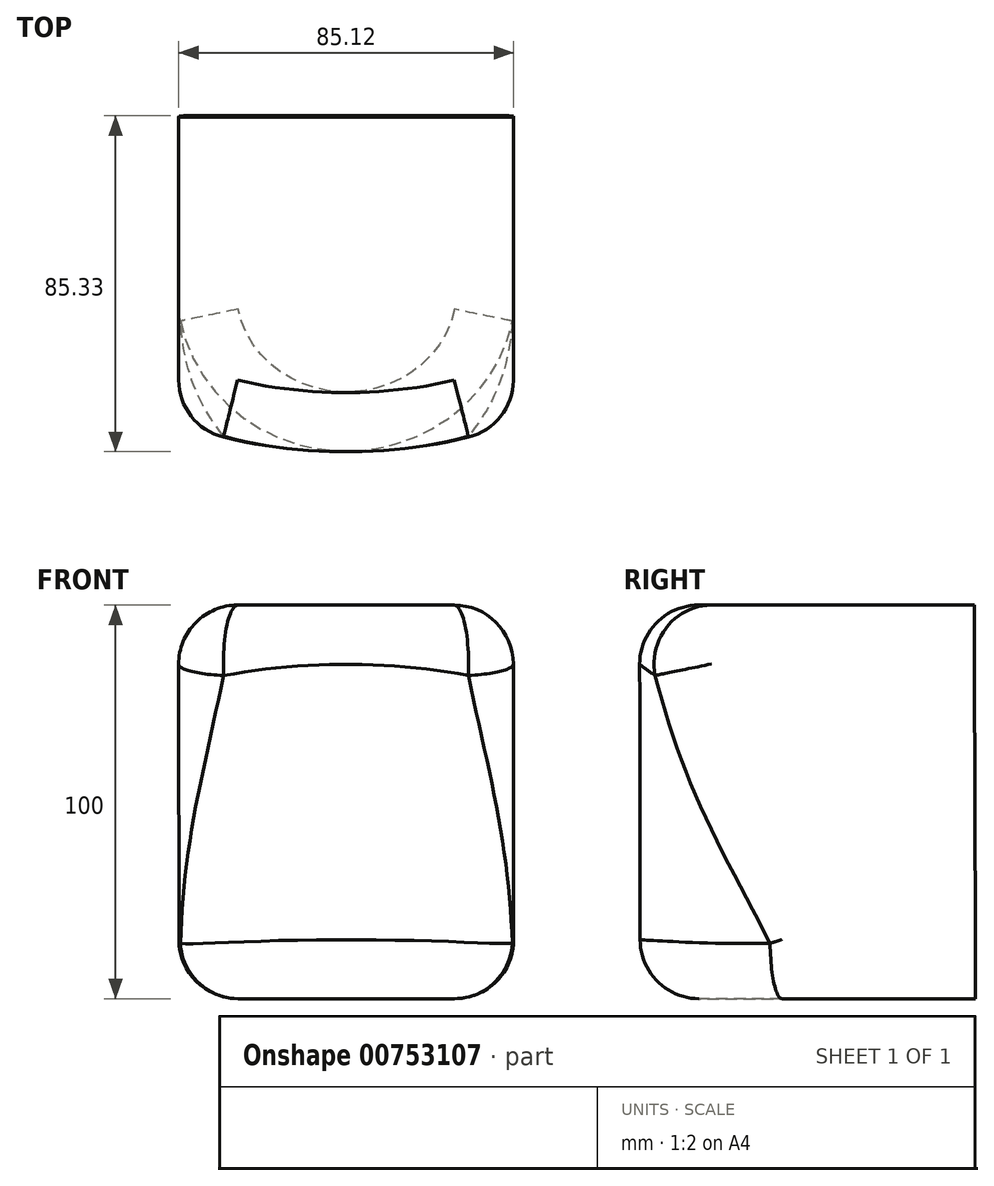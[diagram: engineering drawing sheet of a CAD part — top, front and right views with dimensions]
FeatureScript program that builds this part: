
annotation { "Feature Type Name" : "Feature", "Feature Type Description" : "" }
export const myFeature = defineFeature(function(context is Context, id is Id, definition is map)
    precondition{}
    {
        {
            var Q0;
            Q0=qCreatedBy(makeId("Top.planeOp"),FACE);
            var sketch = newSketch(context, id + "F0", { "sketchPlane" : qUnion([Q0])});
            skLineSegment(sketch, "E0.bottom", {"start": v(-46.57, 25.67) * mm, "end": v(38.43, 25.67) * mm});
            skLineSegment(sketch, "E0.top", {"start": v(-46.57, -59.33) * mm, "end": v(38.43, -59.33) * mm});
            skLineSegment(sketch, "E0.left", {"start": v(-46.57, 25.67) * mm, "end": v(-46.57, -59.33) * mm});
            skLineSegment(sketch, "E0.right", {"start": v(38.43, 25.67) * mm, "end": v(38.43, -59.33) * mm});
            skSolve(sketch);
        }
        {
            var Q0;
            Q0=qCreatedBy(makeId("Top.planeOp"),FACE);
            cPlane(context, id + "F1", {"entities" : qUnion([Q0]), "cplaneType" : CPlaneType.OFFSET, "offset" : 100 * mm, "oppositeDirection" : true, "width" : 150 * mm, "height" : 150 * mm});
        }
        {
            var Q0;
            Q0=qCreatedBy(id+"F1.planeOp",FACE);
            var sketch = newSketch(context, id + "F2", { "sketchPlane" : qUnion([Q0])});
            skLineSegment(sketch, "E1", {"start": v(-46.44, 26.02) * mm, "end": v(-46.44, -18.56) * mm});
            skLineSegment(sketch, "E2", {"start": v(38.59, 26.02) * mm, "end": v(38.59, -18.56) * mm});
            skArc(sketch, "E3", {"start": v(-46.44, -18.56) * mm, "mid": v(-3.93, -59.17) * mm, "end": v(38.59, -18.56) * mm});
            skLineSegment(sketch, "E4", {"start": v(-46.44, 26.02) * mm, "end": v(38.59, 26.02) * mm});
            skSolve(sketch);
        }
        {
            var Q0;
            Q0=makeQuery(id+"F2.imprint","IMPRINT",FACE,{"disambiguationData":[TD([[makeQuery(id+"F2.imprint","IMPRINT",EDGE,{"derivedFrom":sQuery(id+"F2.wireOp",EDGE,"E1")}),1.0]])]});
            var Q1;
            Q1=makeQuery(id+"F0.imprint","IMPRINT",FACE,{"disambiguationData":[TD([[makeQuery(id+"F0.imprint","IMPRINT",EDGE,{"derivedFrom":sQuery(id+"F0.wireOp",EDGE,"E0.bottom")}),-1.0]])]});
            loft(context, id + "F3", {"sheetProfilesArray" : [{ "sheetProfileEntities" : qUnion([Q0]) }, { "sheetProfileEntities" : qUnion([Q1]) }]});
        }
        {
            var Q0;
            Q0=makeQuery(id+"F3.opLoft","MID_CAP_EDGE",EDGE,{"disambiguationData":[OSD([sQuery(id+"F0.wireOp",EDGE,"E0.top"),sQuery(id+"F0.wireOp",EDGE,"E0.left"),sQuery(id+"F0.wireOp",EDGE,"E0.right")])],"capPos":1.0});
            var Q1;
            Q1=makeQuery(id+"F3.opLoft","SWEPT_EDGE",EDGE,{"disambiguationData":[OSD([sQuery(id+"F0.wireOp",EDGE,"E0.top"),sQuery(id+"F0.wireOp",EDGE,"E0.left"),sQuery(id+"F2.wireOp",EDGE,"E1"),sQuery(id+"F2.wireOp",EDGE,"E3")])]});
            var Q2;
            Q2=makeQuery(id+"F3.opLoft","MID_CAP_EDGE",EDGE,{"disambiguationData":[OSD([sQuery(id+"F0.wireOp",EDGE,"E0.bottom"),sQuery(id+"F0.wireOp",EDGE,"E0.top"),sQuery(id+"F0.wireOp",EDGE,"E0.left")])],"capPos":1.0});
            var Q3;
            Q3=makeQuery(id+"F3.opLoft","MID_CAP_EDGE",EDGE,{"disambiguationData":[OSD([sQuery(id+"F0.wireOp",EDGE,"E0.bottom"),sQuery(id+"F0.wireOp",EDGE,"E0.top"),sQuery(id+"F0.wireOp",EDGE,"E0.right")])],"capPos":1.0});
            var Q4;
            Q4=makeQuery(id+"F3.opLoft","SWEPT_EDGE",EDGE,{"disambiguationData":[OSD([sQuery(id+"F0.wireOp",EDGE,"E0.top"),sQuery(id+"F0.wireOp",EDGE,"E0.right"),sQuery(id+"F2.wireOp",EDGE,"E2"),sQuery(id+"F2.wireOp",EDGE,"E3")])]});
            var Q5;
            Q5=makeQuery(id+"F3.opLoft","MID_CAP_EDGE",EDGE,{"disambiguationData":[OSD([sQuery(id+"F2.wireOp",EDGE,"E1"),sQuery(id+"F2.wireOp",EDGE,"E2"),sQuery(id+"F2.wireOp",EDGE,"E3")])],"capPos":0.0});
            var Q6;
            Q6=makeQuery(id+"F3.opLoft","MID_CAP_EDGE",EDGE,{"disambiguationData":[OSD([sQuery(id+"F2.wireOp",EDGE,"E1"),sQuery(id+"F2.wireOp",EDGE,"E3"),sQuery(id+"F2.wireOp",EDGE,"E4")])],"capPos":0.0});
            var Q7;
            Q7=makeQuery(id+"F3.opLoft","MID_CAP_EDGE",EDGE,{"disambiguationData":[OSD([sQuery(id+"F2.wireOp",EDGE,"E2"),sQuery(id+"F2.wireOp",EDGE,"E3"),sQuery(id+"F2.wireOp",EDGE,"E4")])],"capPos":0.0});
            fillet(context, id + "F4", {"entities" : qUnion([Q0, Q1, Q2, Q3, Q4, Q5, Q6, Q7]), "radius" : 15 * mm, "tangentPropagation" : true, "allowEdgeOverflow" : false});
        }
    });
